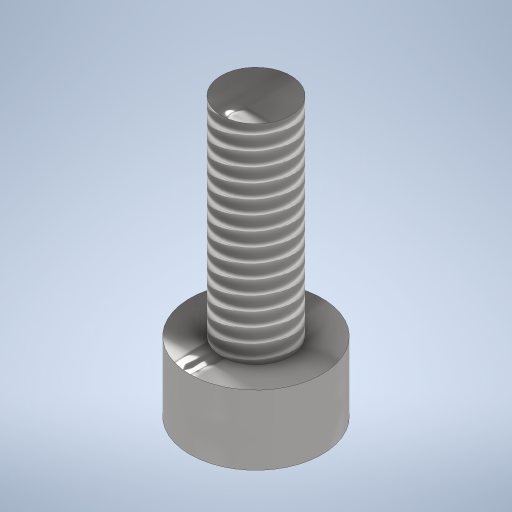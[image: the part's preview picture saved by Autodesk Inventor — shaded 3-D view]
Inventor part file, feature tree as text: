
AUTODESK INVENTOR PART (.ipt)
format: ipt  version: 2024.2 (Build 282272000, 272)  size: 316,416 bytes
history: native  units: mm
features: sketch x2, revolve x1, thread x1, extrude x1
ambient origin geometry x8: Origin, YZ Plane, XZ Plane, XY Plane, X Axis, Y Axis, Z Axis, Center Point
bodies: Solid1 (feature_tree)
feature tree (5):
  revolve  "Revolution1"  [1 undecoded]
  thread  "Thread1"  [1 undecoded]
  extrude  "Extrusion1"  [1 undecoded]
  sketch  "Sketch1"  dims[d4=90.0deg d5=10.0mm d6=0.0mm d0=0.0mm]
  sketch  "Sketch2"
note: 3 required parameter values undecoded (feature->parameter linkage not recoverable at this tier; creation-order binding heuristic only, values carry confidence <= 0.55)